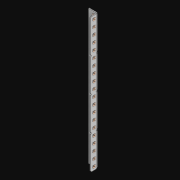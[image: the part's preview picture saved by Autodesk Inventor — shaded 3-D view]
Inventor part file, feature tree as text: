
AUTODESK INVENTOR PART (.ipt)
format: ipt  version: 2021 (Build 250183000, 183)  size: 1,212,416 bytes
history: native  units: in
note: dims shown in document units (in); Inventor stores cm internally (conversion verified against a paired STEP export)
features: extrude x42, other x40, sketch x4, pattern_linear x2, sheet_metal_op x1
ambient origin geometry x8: Origin, YZ Plane, XZ Plane, XY Plane, X Axis, Y Axis, Z Axis, Center Point
bodies: Solid1 (feature_tree)
feature tree (89):
  pattern_linear  "Rectangular Pattern1"  Spacing1=0.5in  [1 undecoded]
  pattern_linear  "Rectangular Pattern3"  Count1=20  [1 undecoded]
  extrude  "Extrusion1"  Depth=0.5in
  extrude  "Extrusion2"  Depth=0.5in
  sketch  "Sketch1"  dims[d0=0.182in]
  other  "Srf1"
  sketch  "Sketch3"  dims[d1=0.063in d2=0.0in]
  other  "Srf3"
  other  "Srf4"
  other  "Srf5"
  other  "Srf6"
  other  "Srf7"
  other  "Srf8"
  other  "Srf9"
  other  "Srf10"
  other  "Srf11"
  other  "Srf12"
  other  "Srf13"
  other  "Srf14"
  other  "Srf15"
  other  "Srf16"
  other  "Srf17"
  other  "Srf18"
  other  "Srf19"
  other  "Srf20"
  other  "Srf21"
  other  "Srf22"
  other  "Srf142"
  other  "Srf143"
  other  "Srf144"
  other  "Srf145"
  other  "Srf146"
  other  "Srf147"
  other  "Srf148"
  other  "Srf149"
  other  "Srf150"
  other  "Srf151"
  other  "Srf152"
  other  "Srf153"
  other  "Srf154"
  other  "Srf155"
  other  "Srf156"
  other  "Srf157"
  other  "Srf158"
  other  "Srf159"
  other  "Srf160"
  sketch  "Sketch4"  dims[d6=0.182in]
  sketch  "Sketch5"  dims[d7=0.063in d8=0.0in d11=0.5in d12=0.3937in d14=0.5in d18=7.874in d20=0.5in d21=7.5in d22=0.0in d23=0.841in d24=0.0in]
  sheet_metal_op  "Fold1"
  extrude  "ExtrusionSrf1"  TaperAngle=0.0deg  [1 undecoded]
  extrude  "ExtrusionSrf3"  Depth=0.5in TaperAngle=0.0deg
  extrude  "ExtrusionSrf4"  [1 undecoded]
  extrude  "ExtrusionSrf5"  [1 undecoded]
  extrude  "ExtrusionSrf6"  [1 undecoded]
  extrude  "ExtrusionSrf7"  [1 undecoded]
  extrude  "ExtrusionSrf8"  [1 undecoded]
  extrude  "ExtrusionSrf9"  [1 undecoded]
  extrude  "ExtrusionSrf10"  [1 undecoded]
  extrude  "ExtrusionSrf11"  [1 undecoded]
  extrude  "ExtrusionSrf12"  [1 undecoded]
  extrude  "ExtrusionSrf13"  [1 undecoded]
  extrude  "ExtrusionSrf14"  [1 undecoded]
  extrude  "ExtrusionSrf15"  [1 undecoded]
  extrude  "ExtrusionSrf16"  [1 undecoded]
  extrude  "ExtrusionSrf17"  [1 undecoded]
  extrude  "ExtrusionSrf18"  [1 undecoded]
  extrude  "ExtrusionSrf19"  [1 undecoded]
  extrude  "ExtrusionSrf20"  [1 undecoded]
  extrude  "ExtrusionSrf21"  [1 undecoded]
  extrude  "ExtrusionSrf22"  [1 undecoded]
  extrude  "ExtrusionSrf142"  [1 undecoded]
  extrude  "ExtrusionSrf143"  [1 undecoded]
  extrude  "ExtrusionSrf144"  [1 undecoded]
  extrude  "ExtrusionSrf145"  [1 undecoded]
  extrude  "ExtrusionSrf146"  [1 undecoded]
  extrude  "ExtrusionSrf147"  [1 undecoded]
  extrude  "ExtrusionSrf148"  [1 undecoded]
  extrude  "ExtrusionSrf149"  [1 undecoded]
  extrude  "ExtrusionSrf150"  [1 undecoded]
  extrude  "ExtrusionSrf151"  [1 undecoded]
  extrude  "ExtrusionSrf152"  [1 undecoded]
  extrude  "ExtrusionSrf153"  [1 undecoded]
  extrude  "ExtrusionSrf154"  [1 undecoded]
  extrude  "ExtrusionSrf155"  [1 undecoded]
  extrude  "ExtrusionSrf156"  [1 undecoded]
  extrude  "ExtrusionSrf157"  [1 undecoded]
  extrude  "ExtrusionSrf158"  [1 undecoded]
  extrude  "ExtrusionSrf159"  [1 undecoded]
  extrude  "ExtrusionSrf160"  [1 undecoded]
note: 41 required parameter values undecoded (feature->parameter linkage not recoverable at this tier; creation-order binding heuristic only, values carry confidence <= 0.55)
